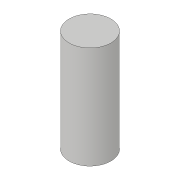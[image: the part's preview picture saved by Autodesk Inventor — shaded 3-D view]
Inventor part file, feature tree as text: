
AUTODESK INVENTOR PART (.ipt)
format: ipt  version: 2017 (Build 210142000, 142)  size: 70,656 bytes
history: native  units: in
note: dims shown in document units (in); Inventor stores cm internally (conversion verified against a paired STEP export)
features: extrude x1, sketch x1
ambient origin geometry x8: Origin, YZ Plane, XZ Plane, XY Plane, X Axis, Y Axis, Z Axis, Center Point
bodies: Solid1 (feature_tree)
feature tree (2):
  extrude  "Extrusion1"  Depth=0.98in TaperAngle=0.0deg
  sketch  "Sketch1"  dims[d0=0.4in d1=0.98in d2=0.0in]
